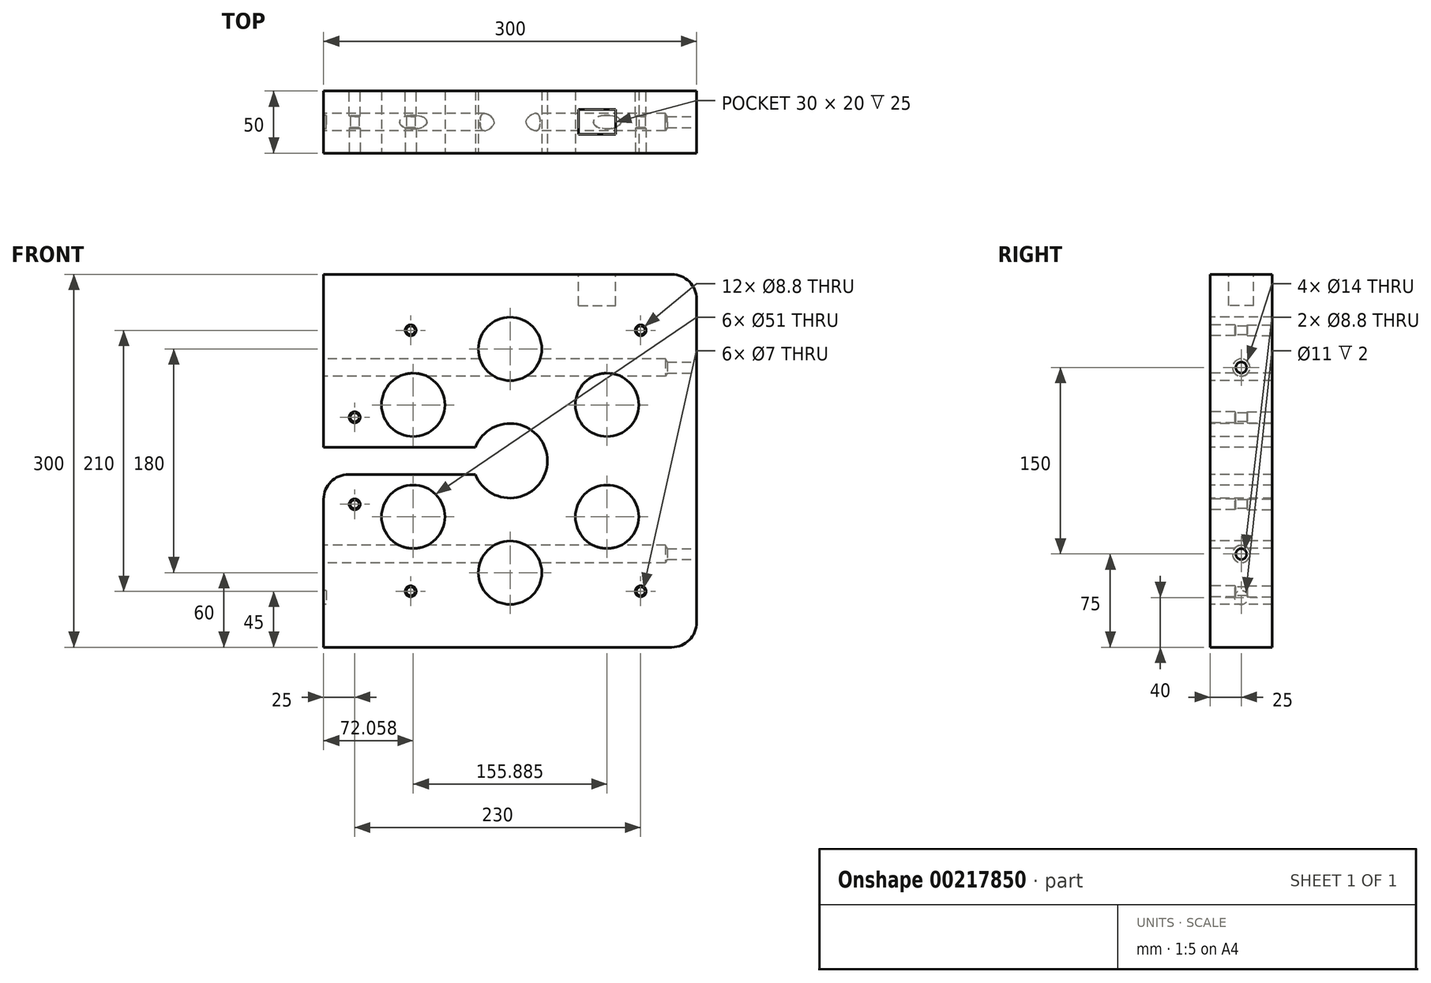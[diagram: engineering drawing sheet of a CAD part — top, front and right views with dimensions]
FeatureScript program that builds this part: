
annotation { "Feature Type Name" : "Feature", "Feature Type Description" : "" }
export const myFeature = defineFeature(function(context is Context, id is Id, definition is map)
    precondition{}
    {
        {
            var Q0;
            Q0=qCreatedBy(makeId("Front.planeOp"),FACE);
            var sketch = newSketch(context, id + "F0", { "sketchPlane" : qUnion([Q0])});
            skLineSegment(sketch, "E0.bottom", {"start": v(-150, 150) * mm, "end": v(150, 150) * mm});
            skLineSegment(sketch, "E0.top", {"start": v(-150, -150) * mm, "end": v(150, -150) * mm});
            skLineSegment(sketch, "E0.left", {"start": v(-150, 150) * mm, "end": v(-150, -150) * mm});
            skLineSegment(sketch, "E0.right", {"start": v(150, 150) * mm, "end": v(150, -150) * mm});
            skPoint(sketch, "E0.middle", {"position": v(0, 0) * mm});
            skSolve(sketch);
        }
        {
            var Q0;
            Q0 = qSketchRegion(id + "F0", true);
            extrude(context, id + "F1", {"entities" : qUnion([Q0]), "depth" : 50 * mm});
        }
        {
            var Q0;
            Q0=makeQuery(id+"F1.opExtrude","CAP_FACE",FACE,{"disambiguationData":[OSD([sQuery(id+"F0.wireOp",EDGE,"E0.bottom"),sQuery(id+"F0.wireOp",EDGE,"E0.top"),sQuery(id+"F0.wireOp",EDGE,"E0.left"),sQuery(id+"F0.wireOp",EDGE,"E0.right")])],"isStart":false});
            var sketch = newSketch(context, id + "F2", { "sketchPlane" : qUnion([Q0])});
            skCircle(sketch, "E1", {"center": v(0, 0) * mm, "radius": 90 * mm});
            skLineSegment(sketch, "E2", {"start": v(0, 0) * mm, "end": v(0, 0) * mm});
            skLineSegment(sketch, "E3", {"start": v(0, 0) * mm, "end": v(0, -110.46) * mm});
            skCircle(sketch, "E4", {"center": v(0, 90) * mm, "radius": 25.5 * mm});
            skCircle(sketch, "E5", {"center": v(0, -90) * mm, "radius": 25.5 * mm});
            skLineSegment(sketch, "E6", {"start": v(0, 0) * mm, "end": v(-107.4, 62) * mm});
            skLineSegment(sketch, "E7", {"start": v(0, 0) * mm, "end": v(96.5, -55.7) * mm});
            skLineSegment(sketch, "E8", {"start": v(0, 0) * mm, "end": v(105.95, 61.17) * mm});
            skLineSegment(sketch, "E9", {"start": v(0, 0) * mm, "end": v(-94.57, -54.6) * mm});
            skLineSegment(sketch, "E10", {"start": v(0, 0) * mm, "end": v(0, 104.5) * mm});
            skCircle(sketch, "E11", {"center": v(-77.94, 45) * mm, "radius": 25.5 * mm});
            skCircle(sketch, "E12", {"center": v(-77.94, -45) * mm, "radius": 25.5 * mm});
            skCircle(sketch, "E13", {"center": v(77.94, -45) * mm, "radius": 25.5 * mm});
            skCircle(sketch, "E14", {"center": v(77.94, 45) * mm, "radius": 25.5 * mm});
            skSolve(sketch);
        }
        {
            var Q0;
            {var subQ0=sQuery(id+"F2.wireOp",EDGE,"E8");var subQ1=sQuery(id+"F2.wireOp",EDGE,"E1");var subQ2=makeQuery(id+"F2.imprint","INTERSECT",VERTEX,{"derivedFrom":[subQ1,subQ0]});Q0=makeQuery(id+"F2.imprint","IMPRINT",FACE,{"disambiguationData":[TD([[makeQuery(id+"F2.imprint","IMPRINT",EDGE,{"disambiguationData":[TD([[subQ2,1.0]])],"derivedFrom":subQ1}),1.0]])]});}
            var Q1;
            {var subQ0=sQuery(id+"F2.wireOp",EDGE,"E8");var subQ1=sQuery(id+"F2.wireOp",EDGE,"E1");var subQ2=makeQuery(id+"F2.imprint","INTERSECT",VERTEX,{"derivedFrom":[subQ1,subQ0]});Q1=makeQuery(id+"F2.imprint","IMPRINT",FACE,{"disambiguationData":[TD([[makeQuery(id+"F2.imprint","IMPRINT",EDGE,{"disambiguationData":[TD([[subQ2,1.0]])],"derivedFrom":subQ1}),-1.0]])]});}
            var Q2;
            {var subQ0=sQuery(id+"F2.wireOp",EDGE,"E8");var subQ1=sQuery(id+"F2.wireOp",EDGE,"E1");var subQ2=makeQuery(id+"F2.imprint","INTERSECT",VERTEX,{"derivedFrom":[subQ1,subQ0]});Q2=makeQuery(id+"F2.imprint","IMPRINT",FACE,{"disambiguationData":[TD([[makeQuery(id+"F2.imprint","IMPRINT",EDGE,{"disambiguationData":[TD([[subQ2,-1.0]])],"derivedFrom":subQ1}),1.0]])]});}
            var Q3;
            {var subQ0=sQuery(id+"F2.wireOp",EDGE,"E8");var subQ1=sQuery(id+"F2.wireOp",EDGE,"E1");var subQ2=makeQuery(id+"F2.imprint","INTERSECT",VERTEX,{"derivedFrom":[subQ1,subQ0]});Q3=makeQuery(id+"F2.imprint","IMPRINT",FACE,{"disambiguationData":[TD([[makeQuery(id+"F2.imprint","IMPRINT",EDGE,{"disambiguationData":[TD([[subQ2,-1.0]])],"derivedFrom":subQ1}),-1.0]])]});}
            var Q4;
            {var subQ0=sQuery(id+"F2.wireOp",EDGE,"E1");var subQ1=makeQuery(id+"F2.imprint","INTERSECT",VERTEX,{"derivedFrom":[subQ0,sQuery(id+"F2.wireOp",EDGE,"E10")]});Q4=makeQuery(id+"F2.imprint","IMPRINT",FACE,{"disambiguationData":[TD([[makeQuery(id+"F2.imprint","IMPRINT",EDGE,{"disambiguationData":[TD([[subQ1,1.0]])],"derivedFrom":subQ0}),-1.0]])]});}
            var Q5;
            {var subQ0=sQuery(id+"F2.wireOp",EDGE,"E10");var subQ1=sQuery(id+"F2.wireOp",EDGE,"E1");var subQ2=makeQuery(id+"F2.imprint","INTERSECT",VERTEX,{"derivedFrom":[subQ1,subQ0]});Q5=makeQuery(id+"F2.imprint","IMPRINT",FACE,{"disambiguationData":[TD([[makeQuery(id+"F2.imprint","IMPRINT",EDGE,{"disambiguationData":[TD([[subQ2,1.0]])],"derivedFrom":subQ1}),1.0]])]});}
            var Q6;
            {var subQ0=sQuery(id+"F2.wireOp",EDGE,"E10");var subQ1=sQuery(id+"F2.wireOp",EDGE,"E1");var subQ2=makeQuery(id+"F2.imprint","INTERSECT",VERTEX,{"derivedFrom":[subQ1,subQ0]});Q6=makeQuery(id+"F2.imprint","IMPRINT",FACE,{"disambiguationData":[TD([[makeQuery(id+"F2.imprint","IMPRINT",EDGE,{"disambiguationData":[TD([[subQ2,-1.0]])],"derivedFrom":subQ1}),1.0]])]});}
            var Q7;
            {var subQ0=sQuery(id+"F2.wireOp",EDGE,"E11");var subQ1=sQuery(id+"F2.wireOp",EDGE,"E1");var subQ2=makeQuery(id+"F2.imprint","INTERSECT",VERTEX,{"disambiguationData":[OD(0.0)],"derivedFrom":[subQ1,subQ0]});Q7=makeQuery(id+"F2.imprint","IMPRINT",FACE,{"disambiguationData":[TD([[makeQuery(id+"F2.imprint","IMPRINT",EDGE,{"disambiguationData":[TD([[subQ2,-1.0]])],"derivedFrom":subQ1}),1.0]])]});}
            var Q8;
            {var subQ0=sQuery(id+"F2.wireOp",EDGE,"E11");var subQ1=sQuery(id+"F2.wireOp",EDGE,"E1");var subQ2=makeQuery(id+"F2.imprint","INTERSECT",VERTEX,{"disambiguationData":[OD(0.0)],"derivedFrom":[subQ1,subQ0]});Q8=makeQuery(id+"F2.imprint","IMPRINT",FACE,{"disambiguationData":[TD([[makeQuery(id+"F2.imprint","IMPRINT",EDGE,{"disambiguationData":[TD([[subQ2,-1.0]])],"derivedFrom":subQ1}),-1.0]])]});}
            var Q9;
            {var subQ0=sQuery(id+"F2.wireOp",EDGE,"E6");var subQ1=sQuery(id+"F2.wireOp",EDGE,"E1");var subQ2=makeQuery(id+"F2.imprint","INTERSECT",VERTEX,{"derivedFrom":[subQ1,subQ0]});Q9=makeQuery(id+"F2.imprint","IMPRINT",FACE,{"disambiguationData":[TD([[makeQuery(id+"F2.imprint","IMPRINT",EDGE,{"disambiguationData":[TD([[subQ2,-1.0]])],"derivedFrom":subQ1}),1.0]])]});}
            var Q10;
            {var subQ0=sQuery(id+"F2.wireOp",EDGE,"E6");var subQ1=sQuery(id+"F2.wireOp",EDGE,"E1");var subQ2=makeQuery(id+"F2.imprint","INTERSECT",VERTEX,{"derivedFrom":[subQ1,subQ0]});Q10=makeQuery(id+"F2.imprint","IMPRINT",FACE,{"disambiguationData":[TD([[makeQuery(id+"F2.imprint","IMPRINT",EDGE,{"disambiguationData":[TD([[subQ2,-1.0]])],"derivedFrom":subQ1}),-1.0]])]});}
            var Q11;
            {var subQ0=sQuery(id+"F2.wireOp",EDGE,"E1");var subQ1=makeQuery(id+"F2.imprint","INTERSECT",VERTEX,{"derivedFrom":[subQ0,sQuery(id+"F2.wireOp",EDGE,"E9")]});Q11=makeQuery(id+"F2.imprint","IMPRINT",FACE,{"disambiguationData":[TD([[makeQuery(id+"F2.imprint","IMPRINT",EDGE,{"disambiguationData":[TD([[subQ1,1.0]])],"derivedFrom":subQ0}),-1.0]])]});}
            var Q12;
            {var subQ0=sQuery(id+"F2.wireOp",EDGE,"E9");var subQ1=sQuery(id+"F2.wireOp",EDGE,"E1");var subQ2=makeQuery(id+"F2.imprint","INTERSECT",VERTEX,{"derivedFrom":[subQ1,subQ0]});Q12=makeQuery(id+"F2.imprint","IMPRINT",FACE,{"disambiguationData":[TD([[makeQuery(id+"F2.imprint","IMPRINT",EDGE,{"disambiguationData":[TD([[subQ2,1.0]])],"derivedFrom":subQ1}),1.0]])]});}
            var Q13;
            {var subQ0=sQuery(id+"F2.wireOp",EDGE,"E9");var subQ1=sQuery(id+"F2.wireOp",EDGE,"E1");var subQ2=makeQuery(id+"F2.imprint","INTERSECT",VERTEX,{"derivedFrom":[subQ1,subQ0]});Q13=makeQuery(id+"F2.imprint","IMPRINT",FACE,{"disambiguationData":[TD([[makeQuery(id+"F2.imprint","IMPRINT",EDGE,{"disambiguationData":[TD([[subQ2,-1.0]])],"derivedFrom":subQ1}),1.0]])]});}
            var Q14;
            {var subQ0=sQuery(id+"F2.wireOp",EDGE,"E1");var subQ1=makeQuery(id+"F2.imprint","INTERSECT",VERTEX,{"derivedFrom":[subQ0,sQuery(id+"F2.wireOp",EDGE,"E3")]});Q14=makeQuery(id+"F2.imprint","IMPRINT",FACE,{"disambiguationData":[TD([[makeQuery(id+"F2.imprint","IMPRINT",EDGE,{"disambiguationData":[TD([[subQ1,1.0]])],"derivedFrom":subQ0}),-1.0]])]});}
            var Q15;
            {var subQ0=sQuery(id+"F2.wireOp",EDGE,"E3");var subQ1=sQuery(id+"F2.wireOp",EDGE,"E1");var subQ2=makeQuery(id+"F2.imprint","INTERSECT",VERTEX,{"derivedFrom":[subQ1,subQ0]});Q15=makeQuery(id+"F2.imprint","IMPRINT",FACE,{"disambiguationData":[TD([[makeQuery(id+"F2.imprint","IMPRINT",EDGE,{"disambiguationData":[TD([[subQ2,1.0]])],"derivedFrom":subQ1}),1.0]])]});}
            var Q16;
            {var subQ0=sQuery(id+"F2.wireOp",EDGE,"E3");var subQ1=sQuery(id+"F2.wireOp",EDGE,"E1");var subQ2=makeQuery(id+"F2.imprint","INTERSECT",VERTEX,{"derivedFrom":[subQ1,subQ0]});Q16=makeQuery(id+"F2.imprint","IMPRINT",FACE,{"disambiguationData":[TD([[makeQuery(id+"F2.imprint","IMPRINT",EDGE,{"disambiguationData":[TD([[subQ2,-1.0]])],"derivedFrom":subQ1}),1.0]])]});}
            var Q17;
            {var subQ0=sQuery(id+"F2.wireOp",EDGE,"E1");var subQ1=makeQuery(id+"F2.imprint","INTERSECT",VERTEX,{"derivedFrom":[subQ0,sQuery(id+"F2.wireOp",EDGE,"E7")]});Q17=makeQuery(id+"F2.imprint","IMPRINT",FACE,{"disambiguationData":[TD([[makeQuery(id+"F2.imprint","IMPRINT",EDGE,{"disambiguationData":[TD([[subQ1,1.0]])],"derivedFrom":subQ0}),-1.0]])]});}
            var Q18;
            {var subQ0=sQuery(id+"F2.wireOp",EDGE,"E7");var subQ1=sQuery(id+"F2.wireOp",EDGE,"E1");var subQ2=makeQuery(id+"F2.imprint","INTERSECT",VERTEX,{"derivedFrom":[subQ1,subQ0]});Q18=makeQuery(id+"F2.imprint","IMPRINT",FACE,{"disambiguationData":[TD([[makeQuery(id+"F2.imprint","IMPRINT",EDGE,{"disambiguationData":[TD([[subQ2,1.0]])],"derivedFrom":subQ1}),1.0]])]});}
            var Q19;
            {var subQ0=sQuery(id+"F2.wireOp",EDGE,"E7");var subQ1=sQuery(id+"F2.wireOp",EDGE,"E1");var subQ2=makeQuery(id+"F2.imprint","INTERSECT",VERTEX,{"derivedFrom":[subQ1,subQ0]});Q19=makeQuery(id+"F2.imprint","IMPRINT",FACE,{"disambiguationData":[TD([[makeQuery(id+"F2.imprint","IMPRINT",EDGE,{"disambiguationData":[TD([[subQ2,-1.0]])],"derivedFrom":subQ1}),1.0]])]});}
            extrude(context, id + "F3", {"entities" : qUnion([Q0, Q1, Q2, Q3, Q4, Q5, Q6, Q7, Q8, Q9, Q10, Q11, Q12, Q13, Q14, Q15, Q16, Q17, Q18, Q19]), "operationType" : NewBodyOperationType.REMOVE, "oppositeDirection" : true, "depth" : 50 * mm});
        }
        {
            var Q0;
            Q0=makeQuery(id+"F1.opExtrude","SWEPT_FACE",FACE,{"disambiguationData":[OSD([sQuery(id+"F0.wireOp",EDGE,"E0.left")])]});
            var sketch = newSketch(context, id + "F4", { "sketchPlane" : qUnion([Q0])});
            skCircle(sketch, "E15", {"center": v(25, -110) * mm, "radius": 5.5 * mm});
            skSolve(sketch);
        }
        {
            var Q0;
            Q0 = qSketchRegion(id + "F4", true);
            extrude(context, id + "F5", {"entities" : qUnion([Q0]), "operationType" : NewBodyOperationType.REMOVE, "oppositeDirection" : true, "depth" : 2 * mm});
        }
        {
            var Q0;
            Q0=makeQuery(id+"F1.opExtrude","CAP_FACE",FACE,{"disambiguationData":[OSD([sQuery(id+"F0.wireOp",EDGE,"E0.bottom"),sQuery(id+"F0.wireOp",EDGE,"E0.top"),sQuery(id+"F0.wireOp",EDGE,"E0.left"),sQuery(id+"F0.wireOp",EDGE,"E0.right")])],"isStart":false});
            var sketch = newSketch(context, id + "F6", { "sketchPlane" : qUnion([Q0])});
            skCircle(sketch, "E16", {"center": v(-80, 105) * mm, "radius": 3.5 * mm});
            skCircle(sketch, "E17", {"center": v(105, 105) * mm, "radius": 3.5 * mm});
            skCircle(sketch, "E18", {"center": v(-80, -105) * mm, "radius": 3.5 * mm});
            skCircle(sketch, "E19", {"center": v(105, -105) * mm, "radius": 3.5 * mm});
            skCircle(sketch, "E20", {"center": v(0, 0) * mm, "radius": 3.5 * mm});
            skCircle(sketch, "E21", {"center": v(-125, 35) * mm, "radius": 3.5 * mm});
            skCircle(sketch, "E22", {"center": v(-125, -35) * mm, "radius": 3.5 * mm});
            skSolve(sketch);
        }
        {
            var Q0;
            Q0 = qSketchRegion(id + "F6", true);
            extrude(context, id + "F7", {"entities" : qUnion([Q0]), "operationType" : NewBodyOperationType.REMOVE, "oppositeDirection" : true, "depth" : 50 * mm});
        }
        {
            var Q0;
            Q0=makeQuery(id+"F1.opExtrude","SWEPT_EDGE",EDGE,{"disambiguationData":[OSD([sQuery(id+"F0.wireOp",EDGE,"E0.bottom"),sQuery(id+"F0.wireOp",EDGE,"E0.right")])]});
            var Q1;
            Q1=makeQuery(id+"F1.opExtrude","SWEPT_EDGE",EDGE,{"disambiguationData":[OSD([sQuery(id+"F0.wireOp",EDGE,"E0.top"),sQuery(id+"F0.wireOp",EDGE,"E0.right")])]});
            fillet(context, id + "F8", {"entities" : qUnion([Q0, Q1]), "radius" : 20 * mm, "tangentPropagation" : true, "allowEdgeOverflow" : false});
        }
        {
            var Q0;
            Q0=makeQuery(id+"F1.opExtrude","CAP_FACE",FACE,{"disambiguationData":[OSD([sQuery(id+"F0.wireOp",EDGE,"E0.bottom"),sQuery(id+"F0.wireOp",EDGE,"E0.top"),sQuery(id+"F0.wireOp",EDGE,"E0.left"),sQuery(id+"F0.wireOp",EDGE,"E0.right")])],"isStart":false});
            var sketch = newSketch(context, id + "F9", { "sketchPlane" : qUnion([Q0])});
            skCircle(sketch, "E23", {"center": v(0, 0) * mm, "radius": 4.5 * mm});
            skCircle(sketch, "E24", {"center": v(-80, 105) * mm, "radius": 4.5 * mm});
            skCircle(sketch, "E25", {"center": v(105, 105) * mm, "radius": 4.5 * mm});
            skCircle(sketch, "E26", {"center": v(-80, -105) * mm, "radius": 4.5 * mm});
            skCircle(sketch, "E27", {"center": v(105, -105) * mm, "radius": 4.5 * mm});
            skCircle(sketch, "E28", {"center": v(-125, 35) * mm, "radius": 4.5 * mm});
            skCircle(sketch, "E29", {"center": v(-125, -35) * mm, "radius": 4.5 * mm});
            skSolve(sketch);
        }
        {
            var Q0;
            Q0=sQuery(id+"F9.wireOp",VERTEX,"E24.center");
            var Q1;
            Q1=sQuery(id+"F9.wireOp",VERTEX,"E25.center");
            var Q2;
            Q2=sQuery(id+"F9.wireOp",VERTEX,"E23.center");
            var Q3;
            Q3=sQuery(id+"F9.wireOp",VERTEX,"E26.center");
            var Q4;
            Q4=sQuery(id+"F9.wireOp",VERTEX,"E27.center");
            var Q5;
            Q5=sQuery(id+"F9.wireOp",VERTEX,"E28.center");
            var Q6;
            Q6=sQuery(id+"F9.wireOp",VERTEX,"E29.center");
            var Q7;
            Q7=makeQuery(id+"F1.opExtrude","SWEPT_BODY",BODY,{"disambiguationData":[OSD([sQuery(id+"F0.wireOp",EDGE,"E0.bottom"),sQuery(id+"F0.wireOp",EDGE,"E0.top"),sQuery(id+"F0.wireOp",EDGE,"E0.left"),sQuery(id+"F0.wireOp",EDGE,"E0.right")])]});
            hole(context, id + "F10", {"style" : HoleStyle.SIMPLE, "endStyle" : HoleEndStyle.BLIND, "standardTappedOrClearance" : lookupTablePath({ "standard" : "ISO", "fit" : "Normal", "size" : "M8", "type" : "Clearance" }), "standardBlindInLast" : lookupTablePath({ "fit" : "Standard", "standard" : "ISO", "size" : "M8", "type" : "Clearance" }), "holeDiameter" : 8.8 * mm, "holeDepth" : 20 * mm, "startFromSketch" : true, "locations" : qUnion([Q0, Q1, Q2, Q3, Q4, Q5, Q6]), "scope" : qUnion([Q7]), "tappedDepth" : 12 * mm, "tapClearance" : 3});
        }
        {
            var Q0;
            Q0=makeQuery(id+"F1.opExtrude","CAP_FACE",FACE,{"disambiguationData":[OSD([sQuery(id+"F0.wireOp",EDGE,"E0.bottom"),sQuery(id+"F0.wireOp",EDGE,"E0.top"),sQuery(id+"F0.wireOp",EDGE,"E0.left"),sQuery(id+"F0.wireOp",EDGE,"E0.right")])],"isStart":true});
            var sketch = newSketch(context, id + "F11", { "sketchPlane" : qUnion([Q0])});
            skCircle(sketch, "E30", {"center": v(-105, 105) * mm, "radius": 3.5 * mm});
            skCircle(sketch, "E31", {"center": v(80, 105) * mm, "radius": 3.5 * mm});
            skCircle(sketch, "E32", {"center": v(0, 0) * mm, "radius": 3.5 * mm});
            skCircle(sketch, "E33", {"center": v(-105, -105) * mm, "radius": 3.5 * mm});
            skCircle(sketch, "E34", {"center": v(80, -105) * mm, "radius": 3.5 * mm});
            skCircle(sketch, "E35", {"center": v(125, 35) * mm, "radius": 3.5 * mm});
            skCircle(sketch, "E36", {"center": v(125, -35) * mm, "radius": 3.5 * mm});
            skSolve(sketch);
        }
        {
            var Q0;
            Q0=sQuery(id+"F11.wireOp",VERTEX,"E30.center");
            var Q1;
            Q1=sQuery(id+"F11.wireOp",VERTEX,"E31.center");
            var Q2;
            Q2=sQuery(id+"F11.wireOp",VERTEX,"E32.center");
            var Q3;
            Q3=sQuery(id+"F11.wireOp",VERTEX,"E33.center");
            var Q4;
            Q4=sQuery(id+"F11.wireOp",VERTEX,"E34.center");
            var Q5;
            Q5=sQuery(id+"F11.wireOp",VERTEX,"E35.center");
            var Q6;
            Q6=sQuery(id+"F11.wireOp",VERTEX,"E36.center");
            var Q7;
            Q7=makeQuery(id+"F1.opExtrude","SWEPT_BODY",BODY,{"disambiguationData":[OSD([sQuery(id+"F0.wireOp",EDGE,"E0.bottom"),sQuery(id+"F0.wireOp",EDGE,"E0.top"),sQuery(id+"F0.wireOp",EDGE,"E0.left"),sQuery(id+"F0.wireOp",EDGE,"E0.right")])]});
            hole(context, id + "F12", {"style" : HoleStyle.SIMPLE, "endStyle" : HoleEndStyle.BLIND, "standardTappedOrClearance" : lookupTablePath({ "standard" : "ISO", "fit" : "Normal", "size" : "M8", "type" : "Clearance" }), "standardBlindInLast" : lookupTablePath({ "fit" : "Standard", "standard" : "ISO", "size" : "M8", "type" : "Clearance" }), "holeDiameter" : 8.8 * mm, "holeDepth" : 20 * mm, "startFromSketch" : true, "locations" : qUnion([Q0, Q1, Q2, Q3, Q4, Q5, Q6]), "scope" : qUnion([Q7]), "tappedDepth" : 12 * mm, "tapClearance" : 3});
        }
        {
            var Q0;
            Q0=makeQuery(id+"F1.opExtrude","CAP_FACE",FACE,{"disambiguationData":[OSD([sQuery(id+"F0.wireOp",EDGE,"E0.bottom"),sQuery(id+"F0.wireOp",EDGE,"E0.top"),sQuery(id+"F0.wireOp",EDGE,"E0.left"),sQuery(id+"F0.wireOp",EDGE,"E0.right")])],"isStart":false});
            var sketch = newSketch(context, id + "F13", { "sketchPlane" : qUnion([Q0])});
            skCircle(sketch, "E37", {"center": v(0, 0) * mm, "radius": 30 * mm});
            skLineSegment(sketch, "E38", {"start": v(0, 0) * mm, "end": v(-150, 0) * mm});
            skLineSegment(sketch, "E39", {"start": v(-150, 11) * mm, "end": v(-12.5, 11) * mm});
            skLineSegment(sketch, "E40", {"start": v(-150, -11) * mm, "end": v(-11.31, -11) * mm});
            skLineSegment(sketch, "E41", {"start": v(-12.5, 11) * mm, "end": v(-11.31, -11) * mm});
            skLineSegment(sketch, "E42", {"start": v(-150, 11) * mm, "end": v(-150, -11) * mm});
            skSolve(sketch);
        }
        {
            var Q0;
            Q0 = qSketchRegion(id + "F13", true);
            extrude(context, id + "F14", {"entities" : qUnion([Q0]), "operationType" : NewBodyOperationType.REMOVE, "oppositeDirection" : true, "depth" : 60 * mm});
        }
        {
            var Q0;
            Q0=makeQuery(id+"F14.boolean.opBoolean","COPY",EDGE,{"derivedFrom":makeQuery(id+"F14.opExtrude","SWEPT_EDGE",EDGE,{"disambiguationData":[OSD([sQuery(id+"F0.wireOp",EDGE,"E0.left"),sQuery(id+"F13.wireOp",EDGE,"E39"),sQuery(id+"F13.wireOp",EDGE,"E42")])]})});
            var Q1;
            Q1=makeQuery(id+"F14.boolean.opBoolean","COPY",EDGE,{"derivedFrom":makeQuery(id+"F14.opExtrude","SWEPT_EDGE",EDGE,{"disambiguationData":[OSD([sQuery(id+"F0.wireOp",EDGE,"E0.left"),sQuery(id+"F13.wireOp",EDGE,"E40"),sQuery(id+"F13.wireOp",EDGE,"E42")])]})});
            fillet(context, id + "F15", {"entities" : qUnion([Q0, Q1]), "radius" : 20 * mm, "tangentPropagation" : true, "allowEdgeOverflow" : false});
        }
        {
            var Q0;
            Q0=makeQuery(id+"F1.opExtrude","SWEPT_FACE",FACE,{"disambiguationData":[OSD([sQuery(id+"F0.wireOp",EDGE,"E0.right")])]});
            var sketch = newSketch(context, id + "F16", { "sketchPlane" : qUnion([Q0])});
            skCircle(sketch, "E43", {"center": v(-25, 75) * mm, "radius": 4.4 * mm});
            skCircle(sketch, "E44", {"center": v(-25, -75) * mm, "radius": 4.4 * mm});
            skSolve(sketch);
        }
        {
            var Q0;
            Q0=sQuery(id+"F16.wireOp",VERTEX,"E43.center");
            var Q1;
            Q1=sQuery(id+"F16.wireOp",VERTEX,"E44.center");
            var Q2;
            Q2=makeQuery(id+"F1.opExtrude","SWEPT_BODY",BODY,{"disambiguationData":[OSD([sQuery(id+"F0.wireOp",EDGE,"E0.bottom"),sQuery(id+"F0.wireOp",EDGE,"E0.top"),sQuery(id+"F0.wireOp",EDGE,"E0.left"),sQuery(id+"F0.wireOp",EDGE,"E0.right")])]});
            hole(context, id + "F17", {"style" : HoleStyle.SIMPLE, "endStyle" : HoleEndStyle.BLIND, "standardTappedOrClearance" : lookupTablePath({ "standard" : "ISO", "fit" : "Normal", "size" : "M8", "type" : "Clearance" }), "standardBlindInLast" : lookupTablePath({ "fit" : "Standard", "standard" : "ISO", "size" : "M8", "type" : "Clearance" }), "holeDiameter" : 8.8 * mm, "holeDepth" : 320 * mm, "tappedDepth" : 12 * mm, "tapClearance" : 3, "startFromSketch" : true, "locations" : qUnion([Q0, Q1]), "scope" : qUnion([Q2])});
        }
        {
            var Q0;
            {var subQ0=sQuery(id+"F0.wireOp",EDGE,"E0.bottom");var subQ2=sQuery(id+"F0.wireOp",EDGE,"E0.left");Q0=makeQuery(id+"F14.boolean.opBoolean","SPLIT",FACE,{"disambiguationData":[TD([makeQuery(id+"F1.opExtrude","SWEPT_FACE",FACE,{"disambiguationData":[OSD([subQ0])]})])],"derivedFrom":makeQuery(id+"F1.opExtrude","SWEPT_FACE",FACE,{"disambiguationData":[OSD([subQ2])]})});}
            var sketch = newSketch(context, id + "F18", { "sketchPlane" : qUnion([Q0])});
            skCircle(sketch, "E45", {"center": v(25, 75) * mm, "radius": 6.5 * mm});
            skCircle(sketch, "E46", {"center": v(25, -75) * mm, "radius": 6.5 * mm});
            skSolve(sketch);
        }
        {
            var Q0;
            Q0=sQuery(id+"F18.wireOp",VERTEX,"E45.center");
            var Q1;
            Q1=sQuery(id+"F18.wireOp",VERTEX,"E46.center");
            var Q2;
            Q2=makeQuery(id+"F1.opExtrude","SWEPT_BODY",BODY,{"disambiguationData":[OSD([sQuery(id+"F0.wireOp",EDGE,"E0.bottom"),sQuery(id+"F0.wireOp",EDGE,"E0.top"),sQuery(id+"F0.wireOp",EDGE,"E0.left"),sQuery(id+"F0.wireOp",EDGE,"E0.right")])]});
            hole(context, id + "F19", {"style" : HoleStyle.SIMPLE, "endStyle" : HoleEndStyle.BLIND, "standardTappedOrClearance" : lookupTablePath({ "standard" : "ISO", "size" : "14", "type" : "Drilled" }), "standardBlindInLast" : lookupTablePath({ "standard" : "ISO", "size" : "14", "type" : "Drilled" }), "holeDiameter" : 14 * mm, "holeDepth" : 275 * mm, "tappedDepth" : 12 * mm, "tapClearance" : 3, "startFromSketch" : true, "locations" : qUnion([Q0, Q1]), "scope" : qUnion([Q2])});
        }
        {
            var Q0;
            Q0=makeQuery(id+"F1.opExtrude","SWEPT_FACE",FACE,{"disambiguationData":[OSD([sQuery(id+"F0.wireOp",EDGE,"E0.bottom")])]});
            var sketch = newSketch(context, id + "F20", { "sketchPlane" : qUnion([Q0])});
            skLineSegment(sketch, "E47.bottom", {"start": v(55, -15) * mm, "end": v(85, -15) * mm});
            skLineSegment(sketch, "E47.top", {"start": v(55, -35) * mm, "end": v(85, -35) * mm});
            skLineSegment(sketch, "E47.left", {"start": v(55, -15) * mm, "end": v(55, -35) * mm});
            skLineSegment(sketch, "E47.right", {"start": v(85, -15) * mm, "end": v(85, -35) * mm});
            skPoint(sketch, "E47.middle", {"position": v(70, -25) * mm});
            skSolve(sketch);
        }
        {
            var Q0;
            Q0 = qSketchRegion(id + "F20", true);
            extrude(context, id + "F21", {"entities" : qUnion([Q0]), "operationType" : NewBodyOperationType.REMOVE, "oppositeDirection" : true, "depth" : 25 * mm});
        }
    });
